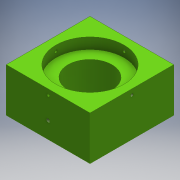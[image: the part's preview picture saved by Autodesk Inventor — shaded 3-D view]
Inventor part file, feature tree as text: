
AUTODESK INVENTOR PART (.ipt)
format: ipt  version: 2016 (Build 200138000, 138)  size: 156,672 bytes
history: native  units: mm
features: sketch x6, extrude x3, hole x3, pattern_circular x1
ambient origin geometry x8: Origin, YZ Plane, XZ Plane, XY Plane, X Axis, Y Axis, Z Axis, Center Point
bodies: Solid1 (feature_tree)
feature tree (13):
  extrude  "baseExtrusion"  Depth=76.2mm
  extrude  "tlExtrusion"  Depth=38.1mm
  extrude  "lightPathExtrusion"  Depth=40.0mm
  hole  "tubeLensGrubScrew1"  [1 undecoded]
  pattern_circular  "tubeLensGrubScrew2"  Count=2 Angle=90.0deg
  hole  "60mmCageSystem"  [1 undecoded]
  hole  "m6MountingHole"  [1 undecoded]
  sketch  "Sketch1"  dims[d0=76.2mm d1=76.2mm]
  sketch  "Sketch2"  dims[d2=38.1mm d3=38.1mm]
  sketch  "Sketch3"  dims[d4=40.0mm d5=0.0mm d6=62.0mm]
  sketch  "Sketch4"  dims[d7=10.0mm d8=0.0mm d9=40.0mm]
  sketch  "Sketch5"  dims[d10=10.0mm d11=0.0mm]
  sketch  "Sketch6"  dims[d12=5.0mm d13=2.459mm d14=6.0mm d15=4.0mm d16=2.0mm d17=90.0deg d18=9.525mm d19=20.594885mm d20=20.0mm d21=90.0deg d23=60.0mm d24=60.0mm d25=30.0mm d26=30.0mm d27=2.156mm d28=5.0mm d29=4.0mm d30=2.0mm d31=90.0deg d32=10.0mm d33=20.594885mm d34=15.0mm d35=3.242mm d36=8.0mm d37=4.0mm d38=2.0mm d39=90.0deg d40=11.8mm d41=20.594885mm]
note: 3 required parameter values undecoded (feature->parameter linkage not recoverable at this tier; creation-order binding heuristic only, values carry confidence <= 0.55)
